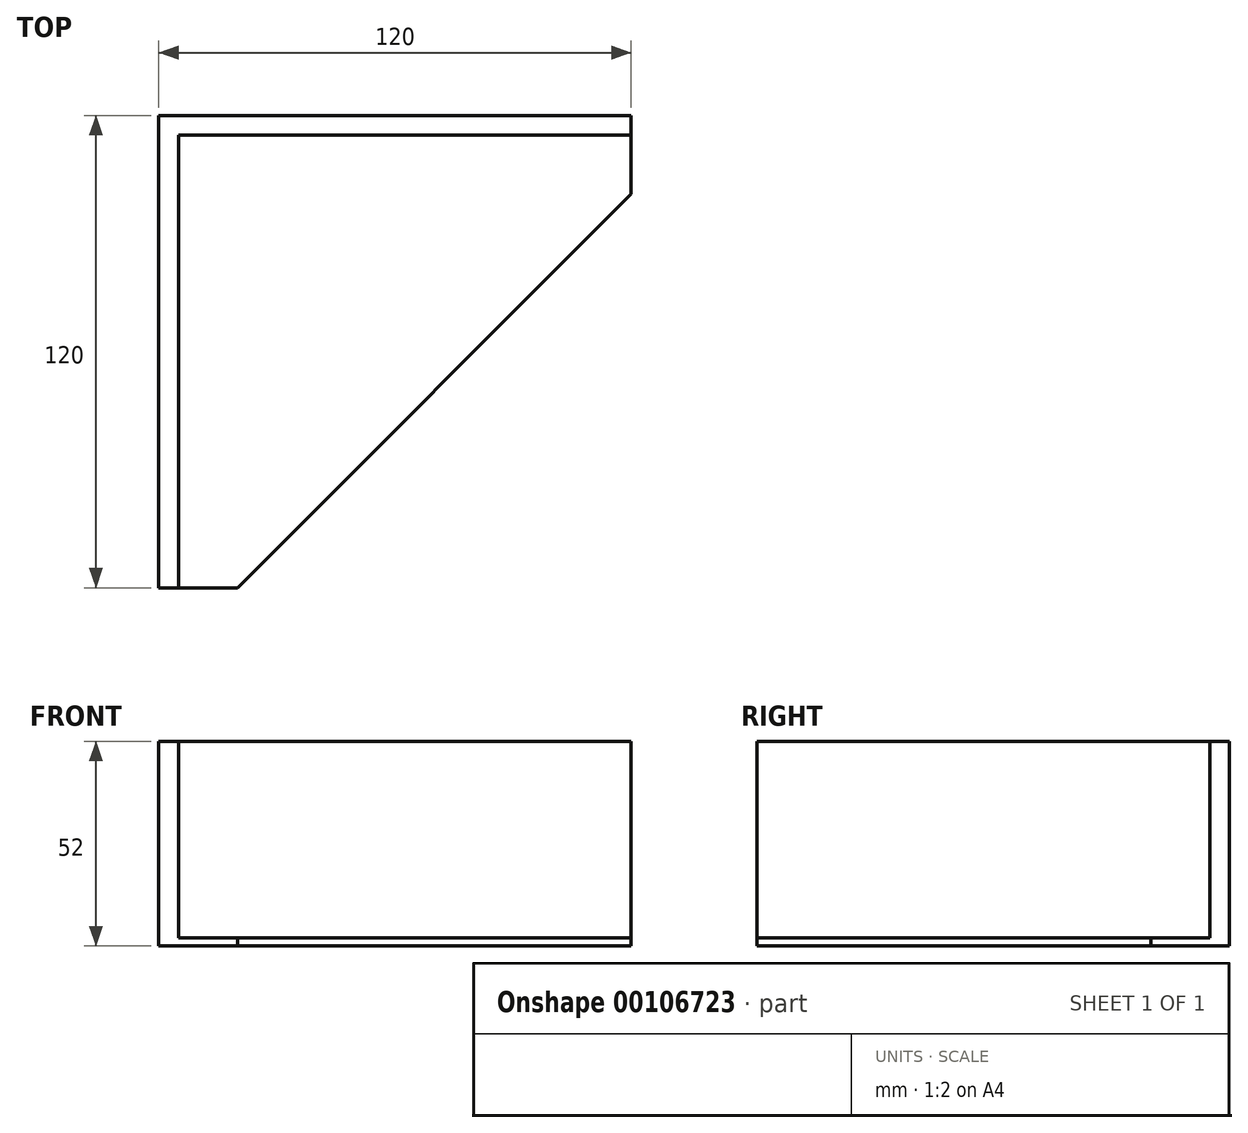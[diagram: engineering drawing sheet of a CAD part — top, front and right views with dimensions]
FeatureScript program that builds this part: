
annotation { "Feature Type Name" : "Feature", "Feature Type Description" : "" }
export const myFeature = defineFeature(function(context is Context, id is Id, definition is map)
    precondition{}
    {
        {
            var Q0;
            Q0=qCreatedBy(makeId("Top.planeOp"),FACE);
            var sketch = newSketch(context, id + "F0", { "sketchPlane" : qUnion([Q0])});
            skLineSegment(sketch, "E0.bottom", {"start": v(-60, 60) * mm, "end": v(60, 60) * mm});
            skLineSegment(sketch, "E0.top", {"start": v(-60, -60) * mm, "end": v(-40, -60) * mm});
            skLineSegment(sketch, "E0.left", {"start": v(-60, 60) * mm, "end": v(-60, -60) * mm});
            skLineSegment(sketch, "E0.right", {"start": v(60, 60) * mm, "end": v(60, 40) * mm});
            skPoint(sketch, "E0.middle", {"position": v(0, 0) * mm});
            skLineSegment(sketch, "E1", {"start": v(-40, -60) * mm, "end": v(60, 40) * mm});
            skPoint(sketch, "E2.orphan", {"position": v(60, -60) * mm});
            skSolve(sketch);
        }
        {
            var Q0;
            Q0 = qSketchRegion(id + "F0", true);
            extrude(context, id + "F1", {"entities" : qUnion([Q0]), "depth" : 2 * mm});
        }
        {
            var Q0;
            Q0=makeQuery(id+"F1.opExtrude","CAP_FACE",FACE,{"disambiguationData":[OSD([sQuery(id+"F0.wireOp",EDGE,"E0.bottom"),sQuery(id+"F0.wireOp",EDGE,"E0.top"),sQuery(id+"F0.wireOp",EDGE,"E0.left"),sQuery(id+"F0.wireOp",EDGE,"E0.right"),sQuery(id+"F0.wireOp",EDGE,"E1")])],"isStart":false});
            var sketch = newSketch(context, id + "F2", { "sketchPlane" : qUnion([Q0])});
            skLineSegment(sketch, "E3.bottom", {"start": v(60, 60) * mm, "end": v(-60, 60) * mm});
            skLineSegment(sketch, "E3.top", {"start": v(60, 55) * mm, "end": v(-55, 55) * mm});
            skLineSegment(sketch, "E3.left", {"start": v(60, 60) * mm, "end": v(60, 55) * mm});
            skLineSegment(sketch, "E3.right", {"start": v(-60, 60) * mm, "end": v(-60, 55) * mm});
            skLineSegment(sketch, "E4.top", {"start": v(-55, -60) * mm, "end": v(-60, -60) * mm});
            skLineSegment(sketch, "E4.left", {"start": v(-55, 55) * mm, "end": v(-55, -60) * mm});
            skLineSegment(sketch, "E4.right", {"start": v(-60, 55) * mm, "end": v(-60, -60) * mm});
            skSolve(sketch);
        }
        {
            var Q0;
            Q0 = qSketchRegion(id + "F2", true);
            extrude(context, id + "F3", {"entities" : qUnion([Q0]), "operationType" : NewBodyOperationType.ADD, "depth" : 50 * mm});
        }
    });
